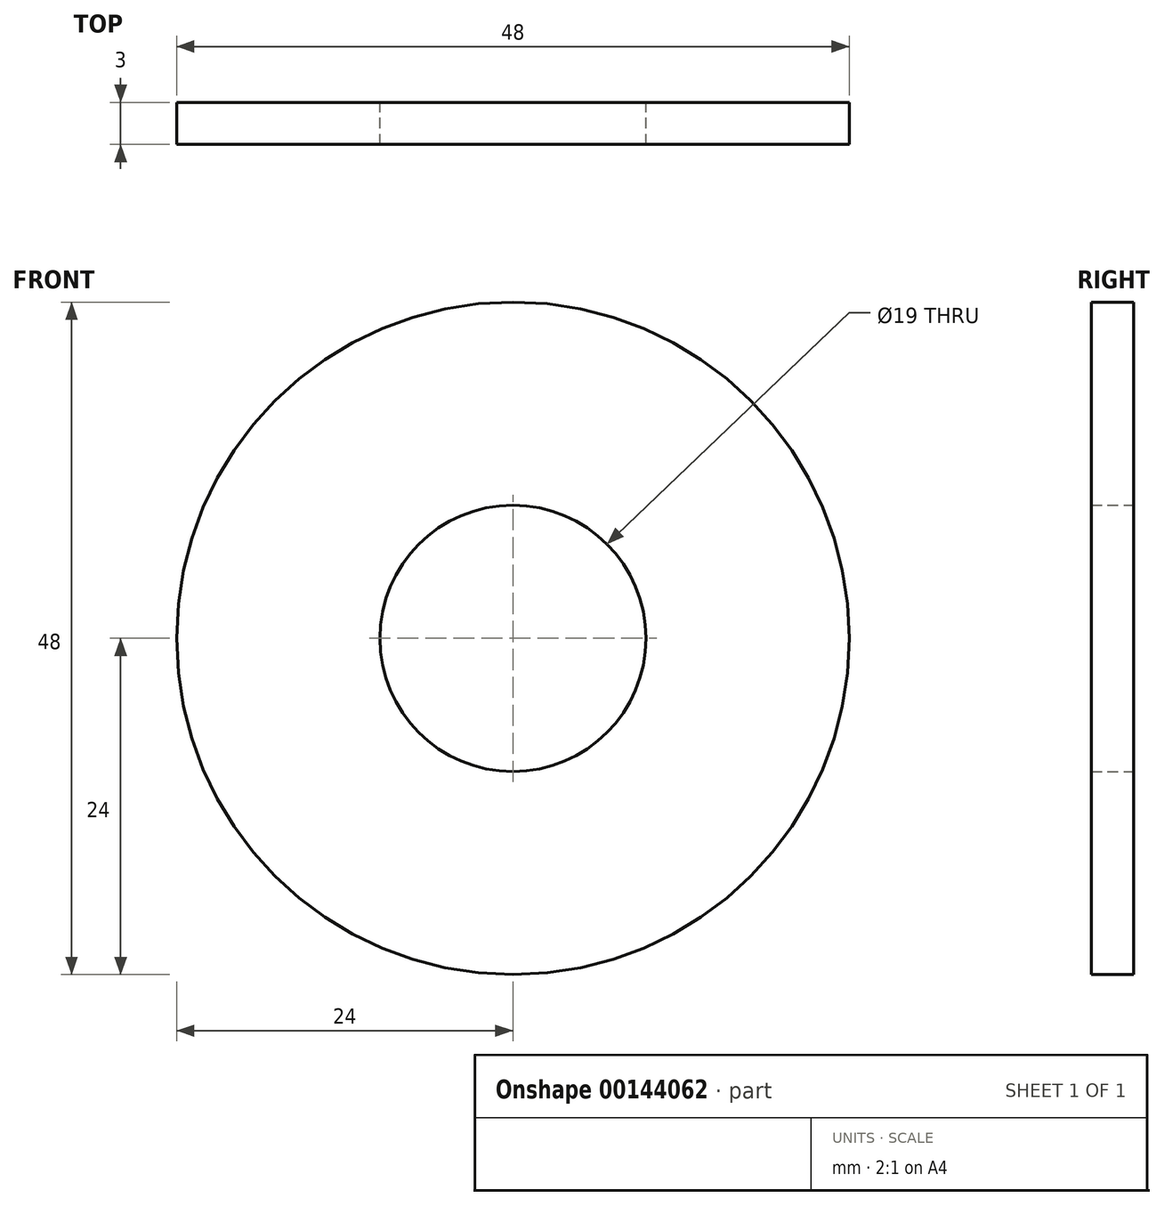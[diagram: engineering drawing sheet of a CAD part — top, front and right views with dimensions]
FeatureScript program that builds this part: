
annotation { "Feature Type Name" : "Feature", "Feature Type Description" : "" }
export const myFeature = defineFeature(function(context is Context, id is Id, definition is map)
    precondition{}
    {
        {
            var Q0;
            Q0=qCreatedBy(makeId("Front.planeOp"),FACE);
            var sketch = newSketch(context, id + "F0", { "sketchPlane" : qUnion([Q0])});
            skCircle(sketch, "E0", {"center": v(0, 0) * mm, "radius": 9.5 * mm});
            skCircle(sketch, "E1", {"center": v(0, 0) * mm, "radius": 24 * mm});
            skSolve(sketch);
        }
        {
            var Q0;
            Q0 = qSketchRegion(id + "F0", true);
            extrude(context, id + "F1", {"entities" : qUnion([Q0]), "depth" : 3 * mm});
        }
    });
